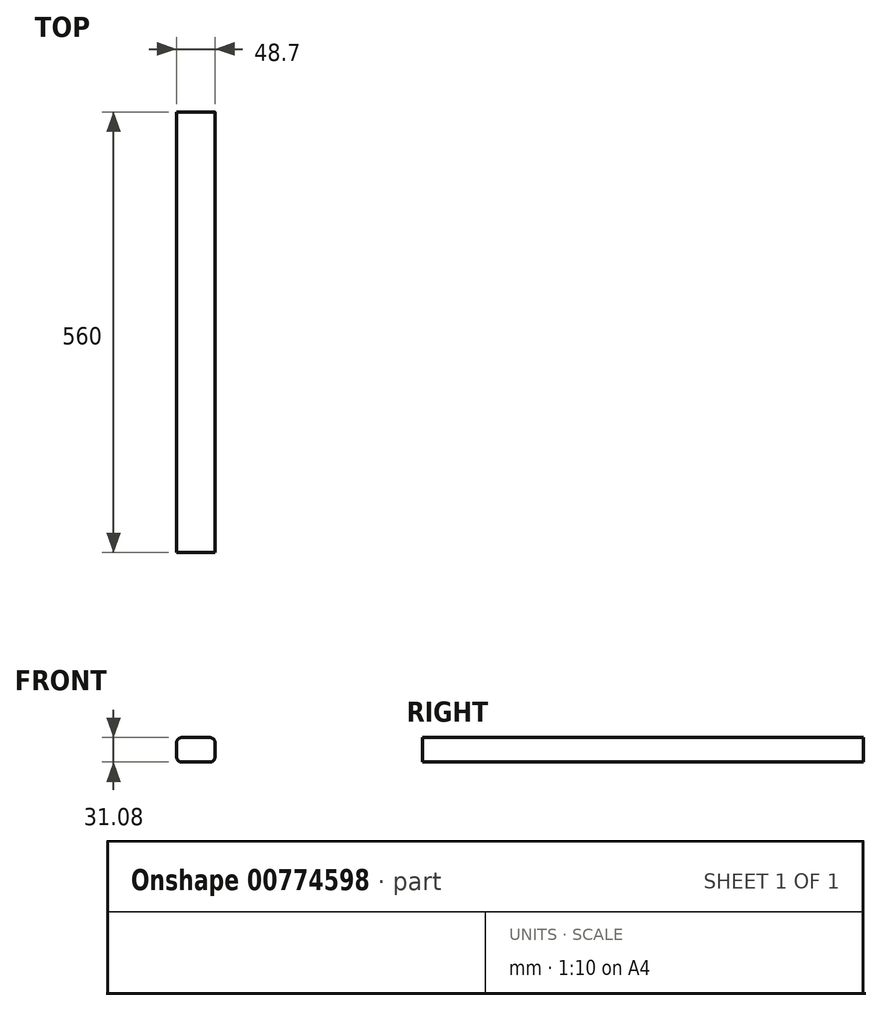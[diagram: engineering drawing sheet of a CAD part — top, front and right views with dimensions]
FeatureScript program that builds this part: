
annotation { "Feature Type Name" : "Feature", "Feature Type Description" : "" }
export const myFeature = defineFeature(function(context is Context, id is Id, definition is map)
    precondition{}
    {
        {
            var Q0;
            Q0=qCreatedBy(makeId("Front.planeOp"),FACE);
            var sketch = newSketch(context, id + "F0", { "sketchPlane" : qUnion([Q0])});
            skLineSegment(sketch, "E0.bottom", {"start": v(18, -15.54) * mm, "end": v(-18, -15.54) * mm});
            skLineSegment(sketch, "E0.top", {"start": v(18, 15.54) * mm, "end": v(-18, 15.54) * mm});
            skLineSegment(sketch, "E0.left", {"start": v(24.35, -9.19) * mm, "end": v(24.35, 9.19) * mm});
            skLineSegment(sketch, "E0.right", {"start": v(-24.35, -9.19) * mm, "end": v(-24.35, 9.19) * mm});
            skPoint(sketch, "E0.middle", {"position": v(0, 0) * mm});
            skPoint(sketch, "E1.visualSharp", {"position": v(-24.35, 15.54) * mm});
            skArc(sketch, "E1.filletArc", {"start": v(-18, 15.54) * mm, "mid": v(-22.49, 13.68) * mm, "end": v(-24.35, 9.19) * mm});
            skPoint(sketch, "E2.visualSharp", {"position": v(24.35, -15.54) * mm});
            skArc(sketch, "E2.filletArc", {"start": v(18, -15.54) * mm, "mid": v(22.49, -13.68) * mm, "end": v(24.35, -9.19) * mm});
            skPoint(sketch, "E3.visualSharp", {"position": v(24.35, 15.54) * mm});
            skArc(sketch, "E3.filletArc", {"start": v(24.35, 9.19) * mm, "mid": v(22.49, 13.68) * mm, "end": v(18, 15.54) * mm});
            skPoint(sketch, "E4.visualSharp", {"position": v(-24.35, -15.54) * mm});
            skArc(sketch, "E4.filletArc", {"start": v(-24.35, -9.19) * mm, "mid": v(-22.49, -13.68) * mm, "end": v(-18, -15.54) * mm});
            skSolve(sketch);
        }
        {
            var Q0;
            Q0=makeQuery(id+"F0.imprint","IMPRINT",FACE,{"disambiguationData":[TD([[makeQuery(id+"F0.imprint","IMPRINT",EDGE,{"derivedFrom":sQuery(id+"F0.wireOp",EDGE,"E0.bottom")}),-1.0]])]});
            extrude(context, id + "F1", {"entities" : qUnion([Q0]), "depth" : 560 * mm, "offsetDistance" : 25.4 * mm});
        }
    });
